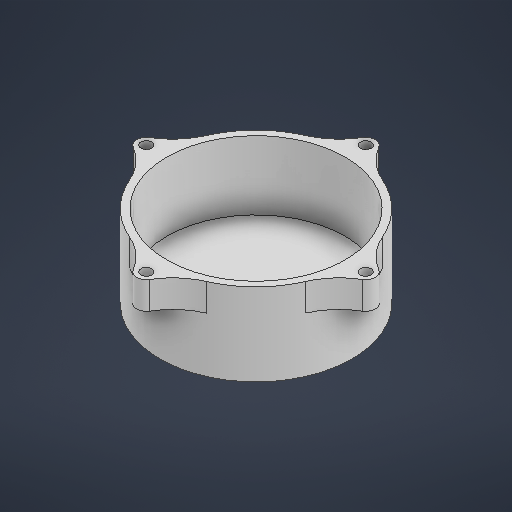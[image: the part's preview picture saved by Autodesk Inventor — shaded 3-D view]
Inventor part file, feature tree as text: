
AUTODESK INVENTOR PART (.ipt)
format: ipt  version: 2025.3 (Build 293356000, 356)  size: 254,464 bytes
history: native  units: mm
features: sketch x3, extrude x3, plane x2
ambient origin geometry x8: Origin, YZ Plane, XZ Plane, XY Plane, X Axis, Y Axis, Z Axis, Center Point
bodies: Body1 (feature_tree)
feature tree (8):
  sketch  "Sketch1"  dims[d0=70.0mm d2=65.0mm]
  extrude  "Extrusion3"  Depth=65.0mm
  extrude  "Extrusion4"  Depth=30.0mm TaperAngle=0.0deg
  plane  "Work Plane1"
  plane  "Work Plane2"
  extrude  "Extrusion9"  Depth=10.0mm
  sketch  "Sketch5"  dims[d19=17.5mm d24=-40.0mm d37=4.0mm d38=7.0mm d40=24.0mm d41=40.0mm d42=40.0mm d44=360.0deg d46=10.0mm d47=0.0mm d25=0.872665mm d26=0.5mm d27=0.872665mm d29=0.5mm d30=0.872665mm d31=0.5mm d32=0.872665mm]
  sketch  "Sketch Circular Pattern1"  dims[d7=5.0mm d8=0.0mm d9=30.0mm d10=0.0mm]
